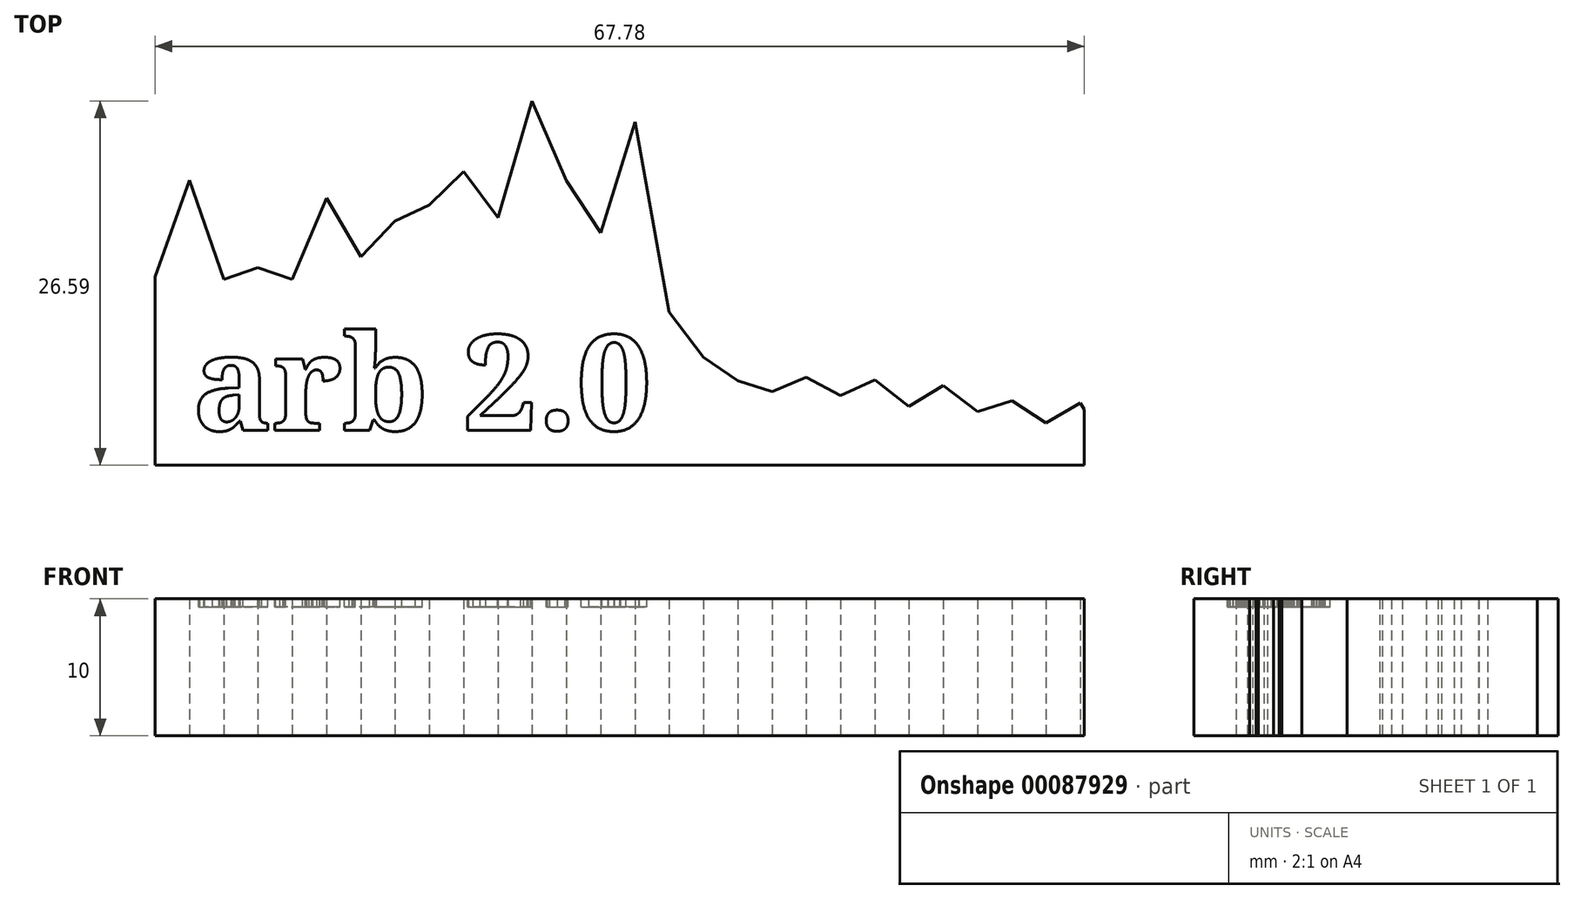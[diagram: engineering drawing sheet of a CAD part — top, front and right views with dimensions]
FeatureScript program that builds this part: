
annotation { "Feature Type Name" : "Feature", "Feature Type Description" : "" }
export const myFeature = defineFeature(function(context is Context, id is Id, definition is map)
    precondition{}
    {
        {
            var Q0;
            Q0=qCreatedBy(makeId("Top.planeOp"),FACE);
            var sketch = newSketch(context, id + "F0", { "sketchPlane" : qUnion([Q0])});
            skLineSegment(sketch, "E0.bottom", {"start": v(-33.89, 26.62) * mm, "end": v(33.89, 26.62) * mm});
            skLineSegment(sketch, "E0.top", {"start": v(-33.89, -0.51) * mm, "end": v(33.89, -0.51) * mm});
            skLineSegment(sketch, "E0.left", {"start": v(-33.89, 26.62) * mm, "end": v(-33.89, -0.51) * mm});
            skLineSegment(sketch, "E0.right", {"start": v(33.89, 26.62) * mm, "end": v(33.89, -0.51) * mm});
            skLineSegment(sketch, "E1", {"start": v(-31.39, 26.62) * mm, "end": v(-31.39, -0.51) * mm, "construction": true});
            skLineSegment(sketch, "E2.1.0.0", {"start": v(-28.89, 26.62) * mm, "end": v(-28.89, -0.51) * mm, "construction": true});
            skLineSegment(sketch, "E2.2.0.0", {"start": v(-26.39, 26.62) * mm, "end": v(-26.39, -0.51) * mm, "construction": true});
            skLineSegment(sketch, "E2.direction1", {"start": v(-31.39, -0.51) * mm, "end": v(-28.89, -0.51) * mm, "construction": true});
            skLineSegment(sketch, "E3.0.3.0", {"start": v(-23.89, 26.62) * mm, "end": v(-23.89, -0.51) * mm, "construction": true});
            skLineSegment(sketch, "E3.0.4.0", {"start": v(-21.39, 26.62) * mm, "end": v(-21.39, -0.51) * mm, "construction": true});
            skLineSegment(sketch, "E3.0.5.0", {"start": v(-18.89, 26.62) * mm, "end": v(-18.89, -0.51) * mm, "construction": true});
            skLineSegment(sketch, "E3.0.6.0", {"start": v(-16.39, 26.62) * mm, "end": v(-16.39, -0.51) * mm, "construction": true});
            skLineSegment(sketch, "E3.0.7.0", {"start": v(-13.89, 26.62) * mm, "end": v(-13.89, -0.51) * mm, "construction": true});
            skLineSegment(sketch, "E3.0.8.0", {"start": v(-11.39, 26.62) * mm, "end": v(-11.39, -0.51) * mm, "construction": true});
            skLineSegment(sketch, "E3.0.9.0", {"start": v(-8.89, 26.62) * mm, "end": v(-8.89, -0.51) * mm, "construction": true});
            skLineSegment(sketch, "E3.0.10.0", {"start": v(-6.39, 26.62) * mm, "end": v(-6.39, -0.51) * mm, "construction": true});
            skLineSegment(sketch, "E3.0.11.0", {"start": v(-3.89, 26.62) * mm, "end": v(-3.89, -0.51) * mm, "construction": true});
            skLineSegment(sketch, "E3.0.12.0", {"start": v(-1.39, 26.62) * mm, "end": v(-1.39, -0.51) * mm, "construction": true});
            skLineSegment(sketch, "E3.0.13.0", {"start": v(1.11, 26.62) * mm, "end": v(1.11, -0.51) * mm, "construction": true});
            skLineSegment(sketch, "E3.0.14.0", {"start": v(3.61, 26.62) * mm, "end": v(3.61, -0.51) * mm, "construction": true});
            skLineSegment(sketch, "E3.0.15.0", {"start": v(6.11, 26.62) * mm, "end": v(6.11, -0.51) * mm, "construction": true});
            skLineSegment(sketch, "E3.0.16.0", {"start": v(8.61, 26.62) * mm, "end": v(8.61, -0.51) * mm, "construction": true});
            skLineSegment(sketch, "E3.0.17.0", {"start": v(11.11, 26.62) * mm, "end": v(11.11, -0.51) * mm, "construction": true});
            skLineSegment(sketch, "E3.0.18.0", {"start": v(13.61, 26.62) * mm, "end": v(13.61, -0.51) * mm, "construction": true});
            skLineSegment(sketch, "E3.0.19.0", {"start": v(16.11, 26.62) * mm, "end": v(16.11, -0.51) * mm, "construction": true});
            skLineSegment(sketch, "E3.0.20.0", {"start": v(18.61, 26.62) * mm, "end": v(18.61, -0.51) * mm, "construction": true});
            skLineSegment(sketch, "E3.0.21.0", {"start": v(21.11, 26.62) * mm, "end": v(21.11, -0.51) * mm, "construction": true});
            skLineSegment(sketch, "E3.0.22.0", {"start": v(23.61, 26.62) * mm, "end": v(23.61, -0.51) * mm, "construction": true});
            skLineSegment(sketch, "E3.0.23.0", {"start": v(26.11, 26.62) * mm, "end": v(26.11, -0.51) * mm, "construction": true});
            skLineSegment(sketch, "E3.0.24.0", {"start": v(28.61, 26.62) * mm, "end": v(28.61, -0.51) * mm, "construction": true});
            skLineSegment(sketch, "E3.0.25.0", {"start": v(31.11, 26.62) * mm, "end": v(31.11, -0.51) * mm, "construction": true});
            skLineSegment(sketch, "E3.0.26.0", {"start": v(33.61, 26.62) * mm, "end": v(33.61, -0.51) * mm, "construction": true});
            skLineSegment(sketch, "E4", {"start": v(-33.89, 13.25) * mm, "end": v(-31.39, 20.28) * mm});
            skLineSegment(sketch, "E5", {"start": v(-31.39, 20.28) * mm, "end": v(-28.89, 13.05) * mm});
            skLineSegment(sketch, "E6", {"start": v(-28.89, 13.05) * mm, "end": v(-26.39, 13.91) * mm});
            skLineSegment(sketch, "E7", {"start": v(-26.39, 13.91) * mm, "end": v(-23.89, 13.05) * mm});
            skLineSegment(sketch, "E8", {"start": v(-23.89, 13.05) * mm, "end": v(-21.39, 19) * mm});
            skLineSegment(sketch, "E9", {"start": v(-21.39, 19) * mm, "end": v(-18.89, 14.7) * mm});
            skLineSegment(sketch, "E10", {"start": v(-18.89, 14.7) * mm, "end": v(-16.39, 17.3) * mm});
            skLineSegment(sketch, "E11", {"start": v(-16.39, 17.3) * mm, "end": v(-13.89, 18.48) * mm});
            skLineSegment(sketch, "E12", {"start": v(-13.89, 18.48) * mm, "end": v(-11.39, 20.92) * mm});
            skLineSegment(sketch, "E13", {"start": v(-11.39, 20.92) * mm, "end": v(-8.89, 17.56) * mm});
            skLineSegment(sketch, "E14", {"start": v(-8.89, 17.56) * mm, "end": v(-6.39, 26.08) * mm});
            skLineSegment(sketch, "E15", {"start": v(-6.39, 26.08) * mm, "end": v(-3.89, 20.27) * mm});
            skLineSegment(sketch, "E16", {"start": v(-3.89, 20.27) * mm, "end": v(-1.39, 16.45) * mm});
            skLineSegment(sketch, "E17", {"start": v(-1.39, 16.45) * mm, "end": v(1.11, 24.55) * mm});
            skLineSegment(sketch, "E18", {"start": v(1.11, 24.55) * mm, "end": v(3.61, 10.66) * mm});
            skLineSegment(sketch, "E19", {"start": v(3.61, 10.66) * mm, "end": v(6.11, 7.36) * mm});
            skLineSegment(sketch, "E20", {"start": v(6.11, 7.36) * mm, "end": v(8.61, 5.65) * mm});
            skLineSegment(sketch, "E21", {"start": v(8.61, 5.65) * mm, "end": v(11.11, 4.85) * mm});
            skLineSegment(sketch, "E22", {"start": v(11.11, 4.85) * mm, "end": v(13.61, 5.91) * mm});
            skLineSegment(sketch, "E23", {"start": v(13.61, 5.91) * mm, "end": v(16.11, 4.59) * mm});
            skLineSegment(sketch, "E24", {"start": v(16.11, 4.59) * mm, "end": v(18.61, 5.71) * mm});
            skLineSegment(sketch, "E25", {"start": v(18.61, 5.71) * mm, "end": v(21.11, 3.77) * mm});
            skLineSegment(sketch, "E26", {"start": v(21.11, 3.77) * mm, "end": v(23.61, 5.31) * mm});
            skLineSegment(sketch, "E27", {"start": v(23.61, 5.31) * mm, "end": v(26.11, 3.4) * mm});
            skLineSegment(sketch, "E28", {"start": v(26.11, 3.4) * mm, "end": v(28.61, 4.18) * mm});
            skLineSegment(sketch, "E29", {"start": v(28.61, 4.18) * mm, "end": v(31.11, 2.57) * mm});
            skLineSegment(sketch, "E30", {"start": v(31.11, 2.57) * mm, "end": v(33.61, 4.02) * mm});
            skLineSegment(sketch, "E31", {"start": v(33.61, 4.02) * mm, "end": v(33.89, 3.55) * mm});
            skLineSegment(sketch, "E32", {"start": v(-33.89, 6.89) * mm, "end": v(-31.39, 6.89) * mm, "construction": true});
            skSolve(sketch);
        }
        {
            var Q0;
            {var subQ2=sQuery(id+"F0.wireOp",EDGE,"E0.top");Q0=makeQuery(id+"F0.imprint","IMPRINT",FACE,{"disambiguationData":[TD([[makeQuery(id+"F0.imprint","IMPRINT",EDGE,{"derivedFrom":subQ2}),1.0]])]});}
            extrude(context, id + "F1", {"entities" : qUnion([Q0]), "depth" : 10 * mm});
        }
        {
            var Q0;
            Q0=makeQuery(id+"F1.opExtrude","CAP_FACE",FACE,{"disambiguationData":[OSD([sQuery(id+"F0.wireOp",EDGE,"E0.top"),sQuery(id+"F0.wireOp",EDGE,"E0.left"),sQuery(id+"F0.wireOp",EDGE,"E0.right"),sQuery(id+"F0.wireOp",EDGE,"E4"),sQuery(id+"F0.wireOp",EDGE,"E5"),sQuery(id+"F0.wireOp",EDGE,"E6"),sQuery(id+"F0.wireOp",EDGE,"E7"),sQuery(id+"F0.wireOp",EDGE,"E8"),sQuery(id+"F0.wireOp",EDGE,"E9"),sQuery(id+"F0.wireOp",EDGE,"E10"),sQuery(id+"F0.wireOp",EDGE,"E11"),sQuery(id+"F0.wireOp",EDGE,"E12"),sQuery(id+"F0.wireOp",EDGE,"E13"),sQuery(id+"F0.wireOp",EDGE,"E14"),sQuery(id+"F0.wireOp",EDGE,"E15"),sQuery(id+"F0.wireOp",EDGE,"E16"),sQuery(id+"F0.wireOp",EDGE,"E17"),sQuery(id+"F0.wireOp",EDGE,"E18"),sQuery(id+"F0.wireOp",EDGE,"E19"),sQuery(id+"F0.wireOp",EDGE,"E20"),sQuery(id+"F0.wireOp",EDGE,"E21"),sQuery(id+"F0.wireOp",EDGE,"E22"),sQuery(id+"F0.wireOp",EDGE,"E23"),sQuery(id+"F0.wireOp",EDGE,"E24"),sQuery(id+"F0.wireOp",EDGE,"E25"),sQuery(id+"F0.wireOp",EDGE,"E26"),sQuery(id+"F0.wireOp",EDGE,"E27"),sQuery(id+"F0.wireOp",EDGE,"E28"),sQuery(id+"F0.wireOp",EDGE,"E29"),sQuery(id+"F0.wireOp",EDGE,"E30"),sQuery(id+"F0.wireOp",EDGE,"E31")])],"isStart":false});
            var sketch = newSketch(context, id + "F2", { "sketchPlane" : qUnion([Q0])});
            skText(sketch, "E33", { "text": "arb 2.0", "fontName": "NotoSerif-Bold.ttf"});
            const initialGuessF2  = {"E33": [-0.03117, 0.00204, 1, 0, 0.007]};
            skSetInitialGuess(sketch, initialGuessF2);
            skSolve(sketch);
        }
        {
            var Q0;
            Q0=makeQuery(id+"F2.imprint","IMPRINT",FACE,{"disambiguationData":[TD([[makeQuery(id+"F2.imprint","IMPRINT",EDGE,{"derivedFrom":sQuery(id+"F2.wireOp",EDGE,"E33.sketch_text.stroke-0")}),-1.0]])]});
            var Q1;
            Q1=makeQuery(id+"F2.imprint","IMPRINT",FACE,{"disambiguationData":[TD([[makeQuery(id+"F2.imprint","IMPRINT",EDGE,{"derivedFrom":sQuery(id+"F2.wireOp",EDGE,"E33.sketch_text.stroke-52")}),-1.0]])]});
            var Q2;
            Q2=makeQuery(id+"F2.imprint","IMPRINT",FACE,{"disambiguationData":[TD([[makeQuery(id+"F2.imprint","IMPRINT",EDGE,{"derivedFrom":sQuery(id+"F2.wireOp",EDGE,"E33.sketch_text.stroke-94")}),-1.0]])]});
            var Q3;
            Q3=makeQuery(id+"F2.imprint","IMPRINT",FACE,{"disambiguationData":[TD([[makeQuery(id+"F2.imprint","IMPRINT",EDGE,{"derivedFrom":sQuery(id+"F2.wireOp",EDGE,"E33.sketch_text.stroke-142")}),-1.0]])]});
            var Q4;
            Q4=makeQuery(id+"F2.imprint","IMPRINT",FACE,{"disambiguationData":[TD([[makeQuery(id+"F2.imprint","IMPRINT",EDGE,{"derivedFrom":sQuery(id+"F2.wireOp",EDGE,"E33.sketch_text.stroke-178")}),-1.0]])]});
            var Q5;
            Q5=makeQuery(id+"F2.imprint","IMPRINT",FACE,{"disambiguationData":[TD([[makeQuery(id+"F2.imprint","IMPRINT",EDGE,{"derivedFrom":sQuery(id+"F2.wireOp",EDGE,"E33.sketch_text.stroke-194")}),-1.0]])]});
            extrude(context, id + "F3", {"entities" : qUnion([Q0, Q1, Q2, Q3, Q4, Q5]), "operationType" : NewBodyOperationType.REMOVE, "oppositeDirection" : true, "depth" : 0.6 * mm});
        }
    });
